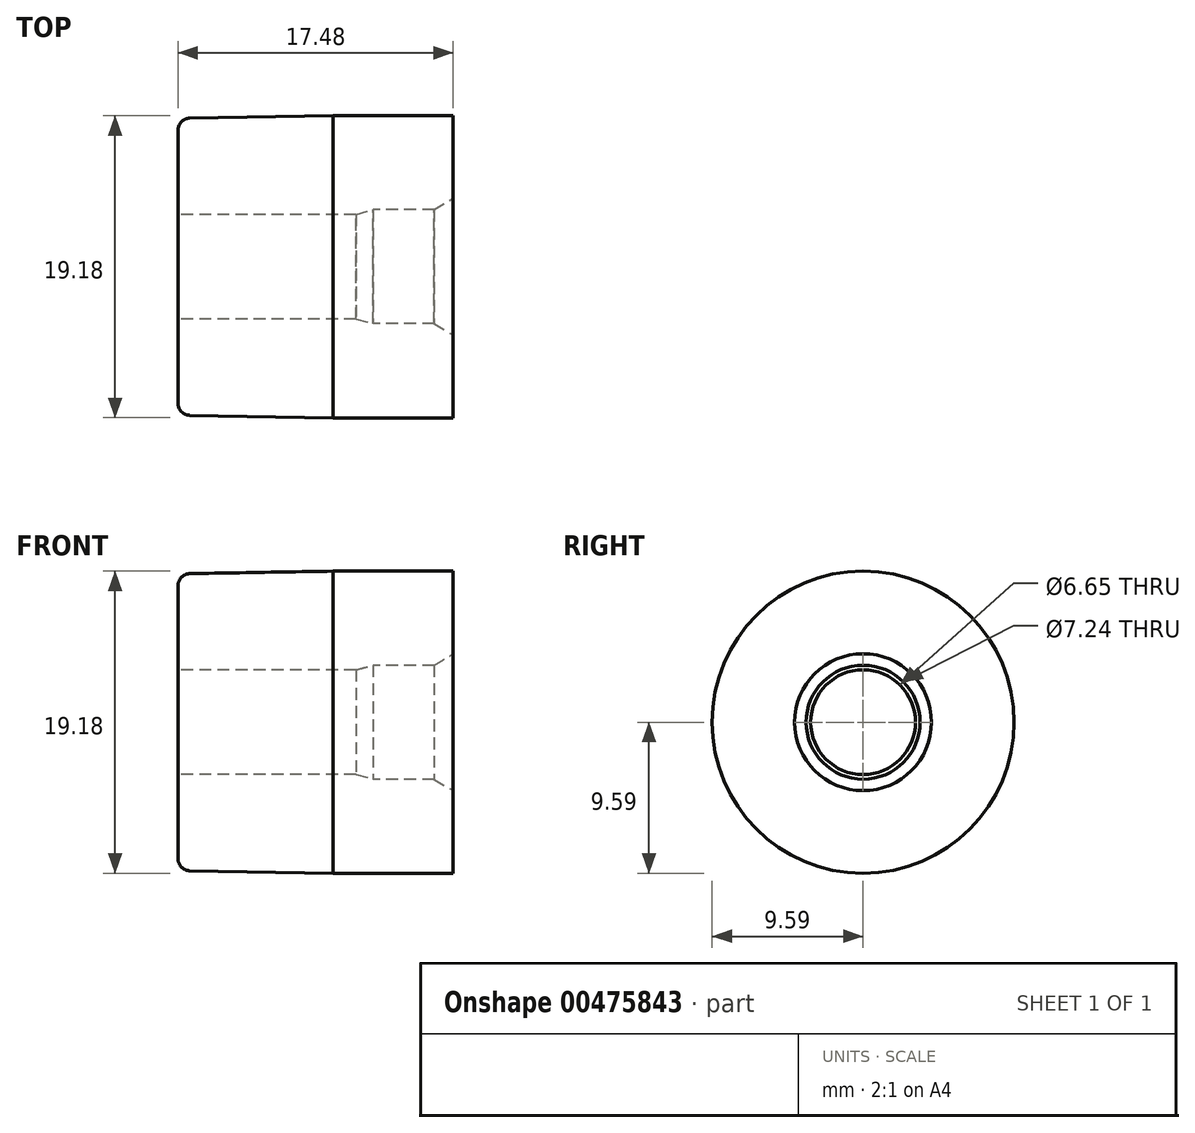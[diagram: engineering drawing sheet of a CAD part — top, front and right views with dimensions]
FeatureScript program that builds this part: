
annotation { "Feature Type Name" : "Feature", "Feature Type Description" : "" }
export const myFeature = defineFeature(function(context is Context, id is Id, definition is map)
    precondition{}
    {
        {
            var Q0;
            Q0=qCreatedBy(makeId("Front.planeOp"),FACE);
            var sketch = newSketch(context, id + "F0", { "sketchPlane" : qUnion([Q0])});
            skLineSegment(sketch, "E0", {"start": v(0, 0) * mm, "end": v(0, 8.67) * mm});
            skLineSegment(sketch, "E1", {"start": v(9.86, 9.6) * mm, "end": v(17.6, 9.6) * mm});
            skLineSegment(sketch, "E2", {"start": v(-6.8, 0) * mm, "end": v(17.6, 0) * mm});
            skLineSegment(sketch, "E3", {"start": v(9.86, 9.6) * mm, "end": v(0.75, 9.44) * mm});
            skPoint(sketch, "E4.visualSharp", {"position": v(0, 9.42) * mm});
            skArc(sketch, "E4.filletArc", {"start": v(0.75, 9.44) * mm, "mid": v(0.22, 9.2) * mm, "end": v(0, 8.67) * mm});
            skLineSegment(sketch, "E5", {"start": v(0, 3.33) * mm, "end": v(11.3, 3.33) * mm});
            skLineSegment(sketch, "E6", {"start": v(11.3, 3.33) * mm, "end": v(12.4, 3.62) * mm});
            skLineSegment(sketch, "E7", {"start": v(12.4, 3.62) * mm, "end": v(16.26, 3.62) * mm});
            skLineSegment(sketch, "E8", {"start": v(16.26, 3.62) * mm, "end": v(17.48, 4.35) * mm});
            skLineSegment(sketch, "E9", {"start": v(17.48, 9.6) * mm, "end": v(17.48, 0) * mm});
            skPoint(sketch, "E10", {"position": v(17.48, 4.35) * mm});
            skSolve(sketch);
        }
        {
            var Q0;
            {var subQ1=sQuery(id+"F0.wireOp",EDGE,"E3");Q0=makeQuery(id+"F0.imprint","IMPRINT",FACE,{"disambiguationData":[TD([[makeQuery(id+"F0.imprint","IMPRINT",EDGE,{"derivedFrom":subQ1}),1.0]])]});}
            var Q1;
            Q1=sQuery(id+"F0.wireOp",EDGE,"E2");
            revolve(context, id + "F1", {"entities" : qUnion([Q0]), "axis" : qUnion([Q1]), "revolveType" : RevolveType.FULL});
        }
    });
